# Revit family: Фитинг подключения L и T-обазных трубок d15
name_source: partatom
category: Соединительные детали трубопроводов
revit_build: Autodesk Revit 2017 (Build: 20160225_1515(x64)
units: mm (PartAtom-declared; Revit-internal decimal feet)

## family parameters
Всегда вертикально = Да
На основе рабочей плоскости = Нет
Общий = Нет
При загрузке вырезать с полостями = Нет
Размер круглого соединителя = Использовать радиус
Тип детали = Соединение

## types (2) — shared parameters
ADSK_Единица измерения = шт
ADSK_Завод-изготовитель = Sanext
DN = 15 мм
R1 = 8 мм
URL = http://sanext.ru
Изготовитель = Sanext
Материал фитинга = DZR латунь
Разработчик = ООО ПРОРУБИМ
Разработчик (телефон) = +7(495)649-85-43
Разработчик модели (URL) = http://prorubim.com
zero-valued in all types: ADSK_Масса

## per-type parameters (varying)
| type | ADSK_Код изделия | DN2 | R2 | a |
| Фитинг подключения L и T-образных трубок d15xG3/4 евроконус | 4937 | 25 мм | 13 мм | 18 мм |
| Фитинг подключения L и T-образных трубок d15xR1/2 c резиновым уплотнителем | 4938 | 20 мм | 10 мм | 28 мм |

note: column(s) folded — value = type name in every type: ADSK_Наименование
